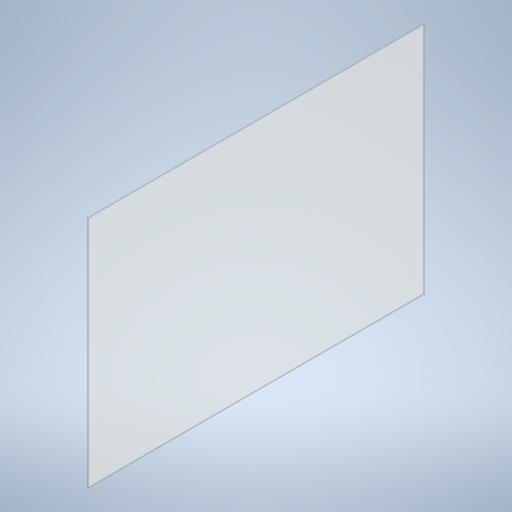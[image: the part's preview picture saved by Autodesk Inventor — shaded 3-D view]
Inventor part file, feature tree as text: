
AUTODESK INVENTOR PART (.ipt)
format: ipt  version: 2024 (Build 280153000, 153)  size: 215,552 bytes
history: native  units: in
note: dims shown in document units (in); Inventor stores cm internally (conversion verified against a paired STEP export)
features: extrude x1, sketch x1
ambient origin geometry x8: Origin, YZ Plane, XZ Plane, XY Plane, X Axis, Y Axis, Z Axis, Center Point
bodies: Solid1 (feature_tree)
feature tree (2):
  extrude  "Extrusion1"  Depth=208.632in
  sketch  "Sketch1"  dims[d2=300.0in d3=208.632in d4=0.75in d5=0.0in]
